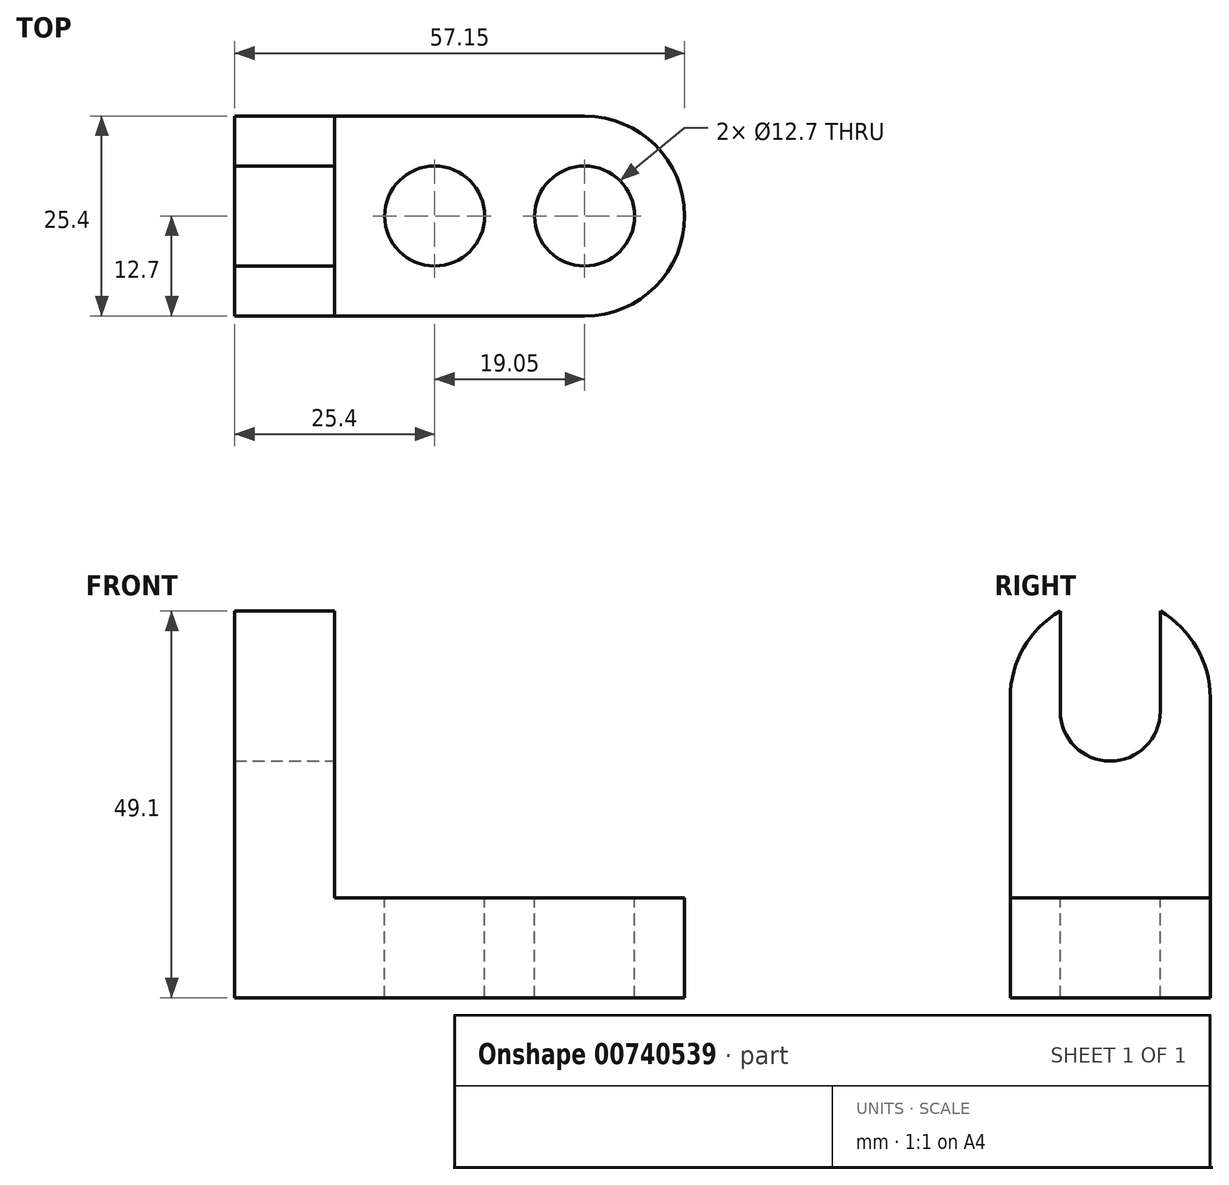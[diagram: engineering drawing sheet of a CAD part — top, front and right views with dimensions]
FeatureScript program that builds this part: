
annotation { "Feature Type Name" : "Feature", "Feature Type Description" : "" }
export const myFeature = defineFeature(function(context is Context, id is Id, definition is map)
    precondition{}
    {
        {
            var Q0;
            Q0=qCreatedBy(makeId("Right.planeOp"),FACE);
            var sketch = newSketch(context, id + "F0", { "sketchPlane" : qUnion([Q0])});
            skLineSegment(sketch, "E0.bottom", {"start": v(0, 0) * mm, "end": v(25.4, 0) * mm});
            skLineSegment(sketch, "E0.top", {"start": v(0, 38.1) * mm, "end": v(25.4, 38.1) * mm});
            skLineSegment(sketch, "E0.left", {"start": v(0, 0) * mm, "end": v(0, 38.1) * mm});
            skLineSegment(sketch, "E0.right", {"start": v(25.4, 0) * mm, "end": v(25.4, 38.1) * mm});
            skCircle(sketch, "E1", {"center": v(12.7, 38.1) * mm, "radius": 12.7 * mm});
            skSolve(sketch);
        }
        {
            var Q0;
            {var subQ0=sQuery(id+"F0.wireOp",EDGE,"E0.top");Q0=makeQuery(id+"F0.imprint","IMPRINT",FACE,{"disambiguationData":[TD([[makeQuery(id+"F0.imprint","IMPRINT",EDGE,{"derivedFrom":subQ0}),1.0]])]});}
            var Q1;
            {var subQ0=sQuery(id+"F0.wireOp",EDGE,"E0.top");Q1=makeQuery(id+"F0.imprint","IMPRINT",FACE,{"disambiguationData":[TD([[makeQuery(id+"F0.imprint","IMPRINT",EDGE,{"derivedFrom":subQ0}),-1.0]])]});}
            var Q2;
            Q2=makeQuery(id+"F0.imprint","IMPRINT",FACE,{"disambiguationData":[TD([[makeQuery(id+"F0.imprint","IMPRINT",EDGE,{"derivedFrom":sQuery(id+"F0.wireOp",EDGE,"E0.bottom")}),1.0]])]});
            extrude(context, id + "F1", {"entities" : qUnion([Q0, Q1, Q2]), "depth" : 12.7 * mm, "offsetDistance" : 25.4 * mm});
        }
        {
            var Q0;
            Q0=makeQuery(id+"F1.opExtrude","CAP_FACE",FACE,{"disambiguationData":[OSD([sQuery(id+"F0.wireOp",EDGE,"E0.bottom"),sQuery(id+"F0.wireOp",EDGE,"E0.left"),sQuery(id+"F0.wireOp",EDGE,"E0.right"),sQuery(id+"F0.wireOp",EDGE,"E1")])],"isStart":false});
            var sketch = newSketch(context, id + "F2", { "sketchPlane" : qUnion([Q0])});
            skLineSegment(sketch, "E2.bottom", {"start": v(6.35, 49.1) * mm, "end": v(19.05, 49.1) * mm});
            skLineSegment(sketch, "E2.top", {"start": v(6.35, 36.4) * mm, "end": v(19.05, 36.4) * mm});
            skLineSegment(sketch, "E2.left", {"start": v(6.35, 49.1) * mm, "end": v(6.35, 36.4) * mm});
            skLineSegment(sketch, "E2.right", {"start": v(19.05, 49.1) * mm, "end": v(19.05, 36.4) * mm});
            skCircle(sketch, "E3", {"center": v(12.7, 36.4) * mm, "radius": 6.35 * mm});
            skSolve(sketch);
        }
        {
            var Q0;
            Q0=makeQuery(id+"F2.imprint","IMPRINT",FACE,{"disambiguationData":[TD([[makeQuery(id+"F2.imprint","IMPRINT",EDGE,{"derivedFrom":sQuery(id+"F2.wireOp",EDGE,"E2.bottom")}),-1.0]])]});
            var Q1;
            {var subQ0=sQuery(id+"F2.wireOp",EDGE,"E2.top");Q1=makeQuery(id+"F2.imprint","IMPRINT",FACE,{"disambiguationData":[TD([[makeQuery(id+"F2.imprint","IMPRINT",EDGE,{"derivedFrom":subQ0}),1.0]])]});}
            var Q2;
            {var subQ0=sQuery(id+"F2.wireOp",EDGE,"E2.top");Q2=makeQuery(id+"F2.imprint","IMPRINT",FACE,{"disambiguationData":[TD([[makeQuery(id+"F2.imprint","IMPRINT",EDGE,{"derivedFrom":subQ0}),-1.0]])]});}
            var Q3;
            {var subQ0=sQuery(id+"F2.wireOp",EDGE,"E2.bottom");Q3=makeQuery(id+"F2.imprint","IMPRINT",FACE,{"disambiguationData":[TD([[makeQuery(id+"F2.imprint","IMPRINT",EDGE,{"derivedFrom":subQ0}),1.0]])]});}
            extrude(context, id + "F3", {"entities" : qUnion([Q0, Q1, Q2, Q3]), "operationType" : NewBodyOperationType.REMOVE, "oppositeDirection" : true, "depth" : 12.7 * mm, "offsetDistance" : 25.4 * mm});
        }
        {
            var Q0;
            Q0=qCreatedBy(makeId("Top.planeOp"),FACE);
            var sketch = newSketch(context, id + "F4", { "sketchPlane" : qUnion([Q0])});
            skLineSegment(sketch, "E4.bottom", {"start": v(12.7, 0) * mm, "end": v(44.45, 0) * mm});
            skLineSegment(sketch, "E4.top", {"start": v(12.7, 25.4) * mm, "end": v(44.45, 25.4) * mm});
            skLineSegment(sketch, "E4.left", {"start": v(12.7, 0) * mm, "end": v(12.7, 25.4) * mm});
            skLineSegment(sketch, "E4.right", {"start": v(44.45, 0) * mm, "end": v(44.45, 25.4) * mm});
            skCircle(sketch, "E5", {"center": v(44.45, 12.7) * mm, "radius": 12.7 * mm});
            skSolve(sketch);
        }
        {
            var Q0;
            {var subQ0=sQuery(id+"F4.wireOp",EDGE,"E4.right");Q0=makeQuery(id+"F4.imprint","IMPRINT",FACE,{"disambiguationData":[TD([[makeQuery(id+"F4.imprint","IMPRINT",EDGE,{"derivedFrom":subQ0}),-1.0]])]});}
            var Q1;
            {var subQ0=sQuery(id+"F4.wireOp",EDGE,"E4.right");Q1=makeQuery(id+"F4.imprint","IMPRINT",FACE,{"disambiguationData":[TD([[makeQuery(id+"F4.imprint","IMPRINT",EDGE,{"derivedFrom":subQ0}),1.0]])]});}
            var Q2;
            {var subQ0=sQuery(id+"F4.wireOp",EDGE,"E4.bottom");Q2=makeQuery(id+"F4.imprint","IMPRINT",FACE,{"disambiguationData":[TD([[makeQuery(id+"F4.imprint","IMPRINT",EDGE,{"derivedFrom":subQ0}),1.0]])]});}
            extrude(context, id + "F5", {"entities" : qUnion([Q0, Q1, Q2]), "operationType" : NewBodyOperationType.ADD, "depth" : 12.7 * mm, "offsetDistance" : 25.4 * mm});
        }
        {
            var Q0;
            Q0=makeQuery(id+"F5.opExtrude","CAP_FACE",FACE,{"disambiguationData":[OSD([sQuery(id+"F4.wireOp",EDGE,"E4.bottom"),sQuery(id+"F4.wireOp",EDGE,"E4.top"),sQuery(id+"F4.wireOp",EDGE,"E4.left"),sQuery(id+"F4.wireOp",EDGE,"E5")])],"isStart":false});
            var sketch = newSketch(context, id + "F6", { "sketchPlane" : qUnion([Q0])});
            skCircle(sketch, "E6", {"center": v(44.45, 12.7) * mm, "radius": 6.35 * mm});
            skCircle(sketch, "E7", {"center": v(25.4, 12.7) * mm, "radius": 6.35 * mm});
            skSolve(sketch);
        }
        {
            var Q0;
            Q0=makeQuery(id+"F6.imprint","IMPRINT",FACE,{"disambiguationData":[TD([[makeQuery(id+"F6.imprint","IMPRINT",EDGE,{"derivedFrom":sQuery(id+"F6.wireOp",EDGE,"E6")}),1.0]])]});
            var Q1;
            Q1=makeQuery(id+"F6.imprint","IMPRINT",FACE,{"disambiguationData":[TD([[makeQuery(id+"F6.imprint","IMPRINT",EDGE,{"derivedFrom":sQuery(id+"F6.wireOp",EDGE,"E7")}),1.0]])]});
            extrude(context, id + "F7", {"entities" : qUnion([Q0, Q1]), "operationType" : NewBodyOperationType.REMOVE, "oppositeDirection" : true, "depth" : 12.7 * mm, "offsetDistance" : 25.4 * mm});
        }
    });
